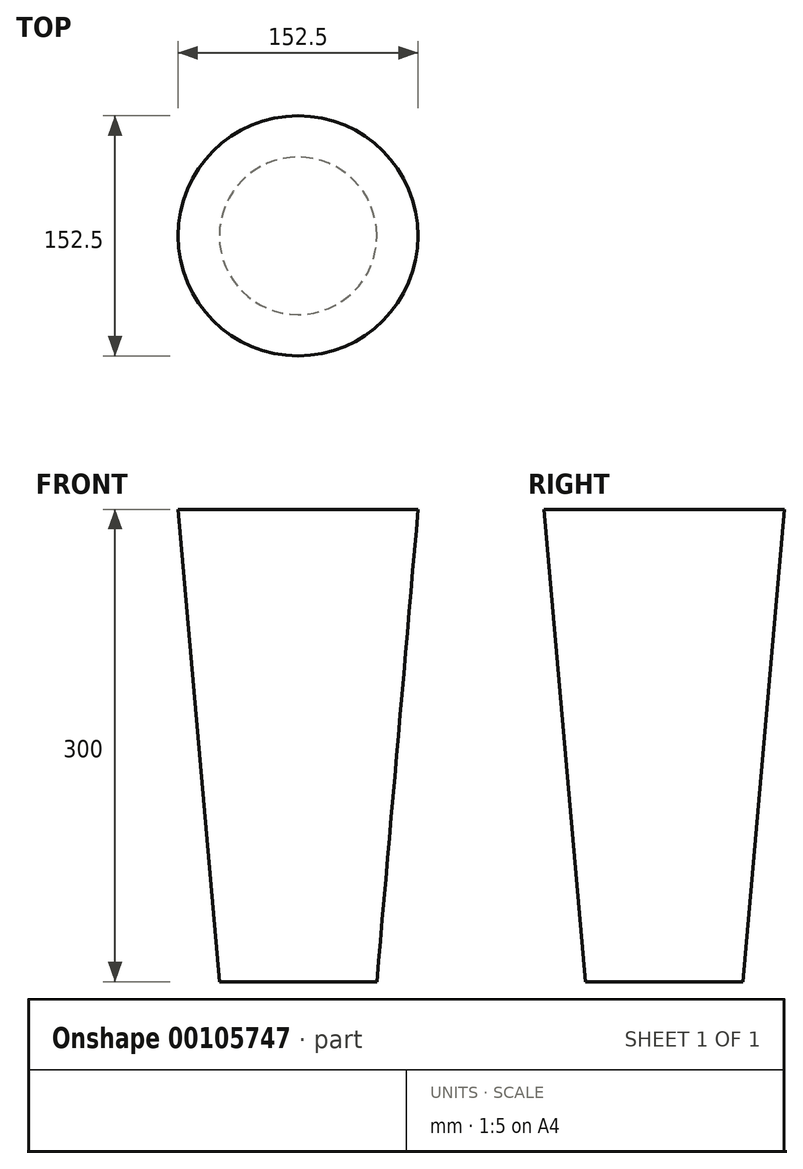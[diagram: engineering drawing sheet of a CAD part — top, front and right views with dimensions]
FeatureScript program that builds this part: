
annotation { "Feature Type Name" : "Feature", "Feature Type Description" : "" }
export const myFeature = defineFeature(function(context is Context, id is Id, definition is map)
    precondition{}
    {
        {
            var Q0;
            Q0=qCreatedBy(makeId("Top.planeOp"),FACE);
            var sketch = newSketch(context, id + "F0", { "sketchPlane" : qUnion([Q0])});
            skCircle(sketch, "E0", {"center": v(0, 0) * mm, "radius": 50 * mm});
            skSolve(sketch);
        }
        {
            var Q0;
            Q0=makeQuery(id+"F0.imprint","IMPRINT",FACE,{"disambiguationData":[TD([[makeQuery(id+"F0.imprint","IMPRINT",EDGE,{"derivedFrom":sQuery(id+"F0.wireOp",EDGE,"E0")}),1.0]])]});
            extrude(context, id + "F1", {"entities" : qUnion([Q0]), "depth" : 300 * mm, "hasDraft" : true, "draftAngle" : 5 * degree});
        }
    });
